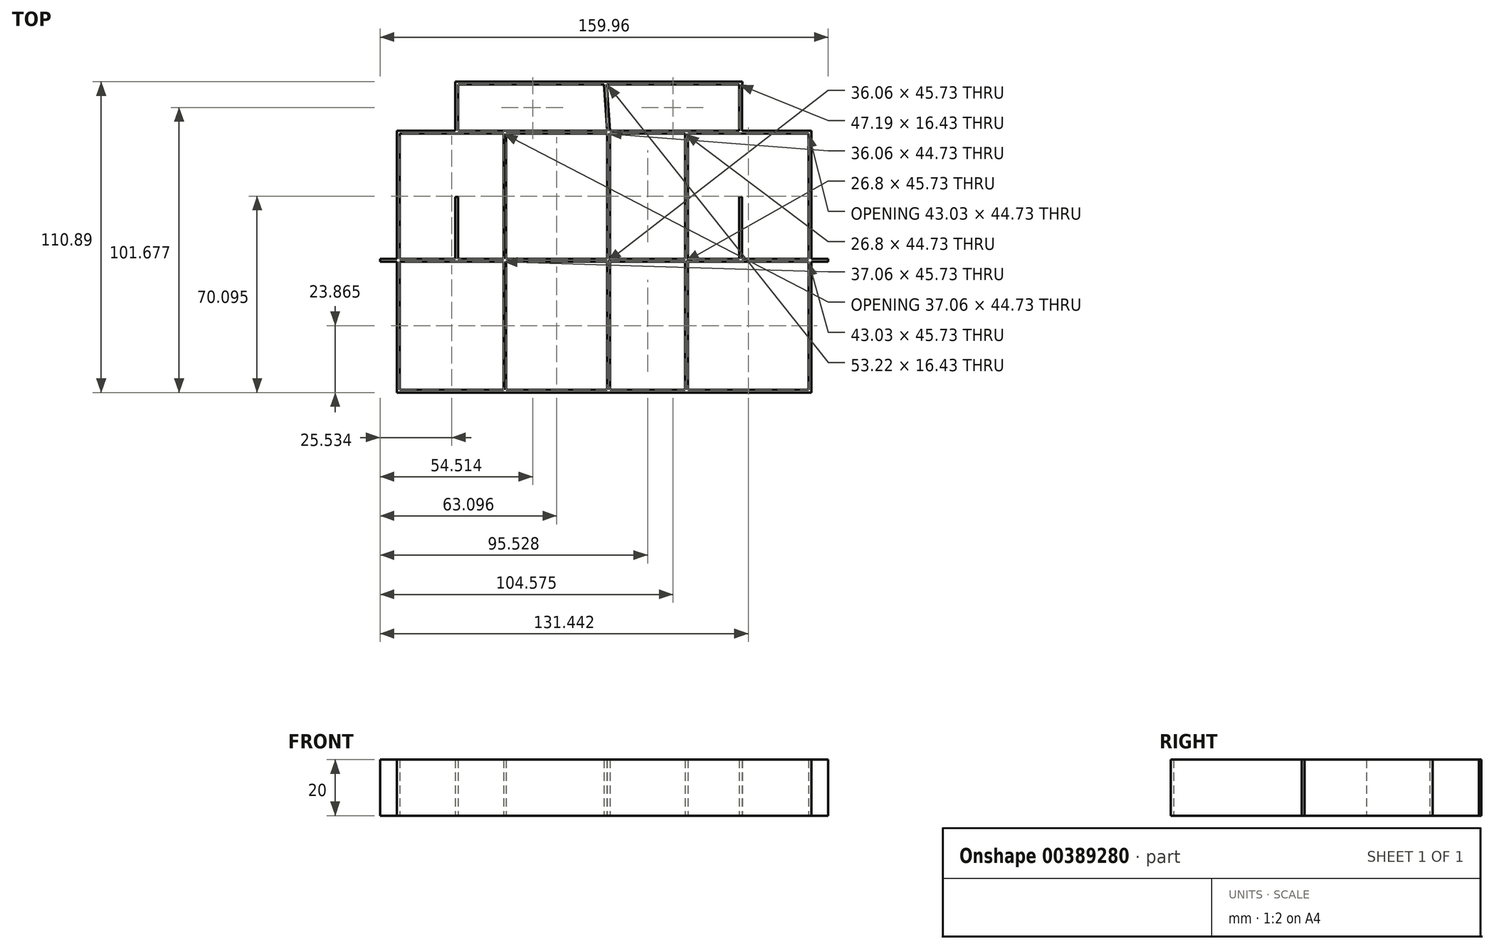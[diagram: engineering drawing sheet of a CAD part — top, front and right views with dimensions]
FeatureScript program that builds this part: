
annotation { "Feature Type Name" : "Feature", "Feature Type Description" : "" }
export const myFeature = defineFeature(function(context is Context, id is Id, definition is map)
    precondition{}
    {
        {
            var Q0;
            Q0=qCreatedBy(makeId("Top.planeOp"),FACE);
            var sketch = newSketch(context, id + "F0", { "sketchPlane" : qUnion([Q0])});
            skCircle(sketch, "E0", {"center": v(0, 0) * mm, "radius": 87.5 * mm});
            skLineSegment(sketch, "E1.bottom", {"start": v(-73.98, 46.73) * mm, "end": v(-53.08, 46.73) * mm});
            skLineSegment(sketch, "E1.top", {"start": v(-73.98, -46.73) * mm, "end": v(73.98, -46.73) * mm});
            skLineSegment(sketch, "E1.left", {"start": v(-73.98, 46.73) * mm, "end": v(-73.98, 1) * mm});
            skLineSegment(sketch, "E1.right", {"start": v(73.98, 46.73) * mm, "end": v(73.98, 1) * mm});
            skLineSegment(sketch, "E2.0", {"start": v(-72.98, 45.73) * mm, "end": v(-35.92, 45.73) * mm});
            skLineSegment(sketch, "E2.1", {"start": v(-72.98, 45.73) * mm, "end": v(-72.98, 1) * mm});
            skLineSegment(sketch, "E2.2", {"start": v(-72.98, -45.73) * mm, "end": v(-35.92, -45.73) * mm});
            skLineSegment(sketch, "E2.3", {"start": v(72.98, 45.73) * mm, "end": v(72.98, 1) * mm});
            skLineSegment(sketch, "E3.bottom", {"start": v(-72.98, 0) * mm, "end": v(-35.92, 0) * mm});
            skLineSegment(sketch, "E3.top", {"start": v(-72.98, 1) * mm, "end": v(-53.08, 1) * mm});
            skLineSegment(sketch, "E4.trimOffspring", {"start": v(-72.98, 0) * mm, "end": v(-72.98, -45.73) * mm});
            skLineSegment(sketch, "E5.trimOffspring", {"start": v(72.98, 0) * mm, "end": v(72.98, -45.73) * mm});
            skLineSegment(sketch, "E6.left", {"start": v(-53.08, 46.73) * mm, "end": v(-53.08, 63.16) * mm});
            skLineSegment(sketch, "E6.right", {"start": v(-52.08, 46.73) * mm, "end": v(-52.08, 63.16) * mm});
            skLineSegment(sketch, "E7.bottom", {"start": v(0, 63.16) * mm, "end": v(1, 63.16) * mm});
            skLineSegment(sketch, "E7.left", {"start": v(0, 63.16) * mm, "end": v(1.15, 46.73) * mm});
            skLineSegment(sketch, "E7.right", {"start": v(1, 63.16) * mm, "end": v(2.15, 46.73) * mm});
            skLineSegment(sketch, "E8.bottom", {"start": v(48.2, 63.16) * mm, "end": v(49.2, 63.16) * mm});
            skLineSegment(sketch, "E8.left", {"start": v(48.2, 63.16) * mm, "end": v(48.2, 46.73) * mm});
            skLineSegment(sketch, "E8.right", {"start": v(49.2, 63.16) * mm, "end": v(49.2, 46.73) * mm});
            skLineSegment(sketch, "E9.trimOffspring", {"start": v(-52.08, 46.73) * mm, "end": v(1.15, 46.73) * mm});
            skLineSegment(sketch, "E10.trimOffspring", {"start": v(2.15, 46.73) * mm, "end": v(48.2, 46.73) * mm});
            skLineSegment(sketch, "E11.trimOffspring", {"start": v(49.2, 46.73) * mm, "end": v(73.98, 46.73) * mm});
            skLineSegment(sketch, "E12.bottom", {"start": v(-73.98, 0) * mm, "end": v(-79.98, 0) * mm});
            skLineSegment(sketch, "E12.top", {"start": v(-73.98, 1) * mm, "end": v(-79.98, 1) * mm});
            skLineSegment(sketch, "E12.right", {"start": v(-79.98, 0) * mm, "end": v(-79.98, 1) * mm});
            skPoint(sketch, "E13.firstSnap0", {"position": v(73.98, 0) * mm});
            skPoint(sketch, "E13.oppositeSnap0", {"position": v(-76.98, 1) * mm});
            skLineSegment(sketch, "E13.bottom", {"start": v(73.98, 0) * mm, "end": v(79.98, 0) * mm});
            skLineSegment(sketch, "E13.top", {"start": v(73.98, 1) * mm, "end": v(79.98, 1) * mm});
            skLineSegment(sketch, "E13.right", {"start": v(79.98, 0) * mm, "end": v(79.98, 1) * mm});
            skLineSegment(sketch, "E14.trimOffspring", {"start": v(73.98, 0) * mm, "end": v(73.98, -46.73) * mm});
            skLineSegment(sketch, "E15.trimOffspring", {"start": v(-73.98, 0) * mm, "end": v(-73.98, -46.73) * mm});
            skLineSegment(sketch, "E16.left", {"start": v(1.15, 46.73) * mm, "end": v(1.15, -45.73) * mm});
            skLineSegment(sketch, "E16.right", {"start": v(2.15, 46.73) * mm, "end": v(2.15, -45.73) * mm});
            skLineSegment(sketch, "E17.trimOffspring", {"start": v(2.15, 45.73) * mm, "end": v(72.98, 45.73) * mm});
            skLineSegment(sketch, "E18.trimOffspring", {"start": v(2.15, 1) * mm, "end": v(28.95, 1) * mm});
            skLineSegment(sketch, "E19.trimOffspring", {"start": v(2.15, 0) * mm, "end": v(28.95, 0) * mm});
            skLineSegment(sketch, "E20.trimOffspring", {"start": v(2.15, -45.73) * mm, "end": v(28.95, -45.73) * mm});
            skLineSegment(sketch, "E21.top", {"start": v(-53.08, 23.07) * mm, "end": v(-52.08, 23.07) * mm});
            skLineSegment(sketch, "E21.left", {"start": v(-53.08, 1) * mm, "end": v(-53.08, 23.07) * mm});
            skLineSegment(sketch, "E21.right", {"start": v(-52.08, 1) * mm, "end": v(-52.08, 23.07) * mm});
            skLineSegment(sketch, "E22.top", {"start": v(49.2, 23.07) * mm, "end": v(48.2, 23.07) * mm});
            skLineSegment(sketch, "E22.left", {"start": v(49.2, 1) * mm, "end": v(49.2, 23.07) * mm});
            skLineSegment(sketch, "E22.right", {"start": v(48.2, 1) * mm, "end": v(48.2, 23.07) * mm});
            skLineSegment(sketch, "E23.trimOffspring", {"start": v(-52.08, 1) * mm, "end": v(-35.92, 1) * mm});
            skLineSegment(sketch, "E24.trimOffspring", {"start": v(49.2, 1) * mm, "end": v(72.98, 1) * mm});
            skLineSegment(sketch, "E25.bottom", {"start": v(-52.08, 63.16) * mm, "end": v(49.41, 63.16) * mm});
            skLineSegment(sketch, "E25.top", {"start": v(-53.08, 64.16) * mm, "end": v(49.41, 64.16) * mm});
            skLineSegment(sketch, "E25.left", {"start": v(-53.08, 63.16) * mm, "end": v(-53.08, 64.16) * mm});
            skLineSegment(sketch, "E25.right", {"start": v(49.41, 63.16) * mm, "end": v(49.41, 64.16) * mm});
            skLineSegment(sketch, "E26.left", {"start": v(-35.92, 45.73) * mm, "end": v(-35.92, -45.73) * mm});
            skLineSegment(sketch, "E26.right", {"start": v(-34.92, 45.73) * mm, "end": v(-34.92, -45.73) * mm});
            skLineSegment(sketch, "E27.bottom", {"start": v(28.95, 45.73) * mm, "end": v(29.95, 45.73) * mm});
            skLineSegment(sketch, "E27.left", {"start": v(28.95, 45.73) * mm, "end": v(28.95, 1) * mm});
            skLineSegment(sketch, "E27.right", {"start": v(29.95, 45.73) * mm, "end": v(29.95, 1) * mm});
            skLineSegment(sketch, "E28.trimOffspring", {"start": v(-34.92, 45.73) * mm, "end": v(1.15, 45.73) * mm});
            skLineSegment(sketch, "E29.trimOffspring", {"start": v(-34.92, 1) * mm, "end": v(1.15, 1) * mm});
            skLineSegment(sketch, "E30.trimOffspring", {"start": v(-34.92, 0) * mm, "end": v(0, 0) * mm});
            skLineSegment(sketch, "E31.trimOffspring", {"start": v(-34.92, -45.73) * mm, "end": v(1.15, -45.73) * mm});
            skLineSegment(sketch, "E32.trimOffspring", {"start": v(29.95, -45.73) * mm, "end": v(72.98, -45.73) * mm});
            skLineSegment(sketch, "E33.trimOffspring", {"start": v(29.95, 1) * mm, "end": v(48.2, 1) * mm});
            skLineSegment(sketch, "E34.trimOffspring", {"start": v(28.95, 0) * mm, "end": v(28.95, -45.73) * mm});
            skLineSegment(sketch, "E35.trimOffspring", {"start": v(29.95, 0) * mm, "end": v(72.98, 0) * mm});
            skLineSegment(sketch, "E36.trimOffspring", {"start": v(29.95, 0) * mm, "end": v(29.95, -45.73) * mm});
            skLineSegment(sketch, "E37", {"start": v(0, 0) * mm, "end": v(1.15, 0) * mm});
            skPoint(sketch, "E37.endSnap0", {"position": v(1.15, 0.5) * mm});
            skSolve(sketch);
        }
        {
            var Q0;
            {var subQ0=sQuery(id+"F0.wireOp",EDGE,"E1.bottom");var subQ1=sQuery(id+"F0.wireOp",EDGE,"E0");var subQ2=makeQuery(id+"F0.imprint","INTERSECT",VERTEX,{"derivedFrom":[subQ1,subQ0]});Q0=makeQuery(id+"F0.imprint","IMPRINT",FACE,{"disambiguationData":[TD([[makeQuery(id+"F0.imprint","IMPRINT",EDGE,{"disambiguationData":[TD([[subQ2,1.0]])],"derivedFrom":subQ1}),-1.0]])]});}
            var Q1;
            {var subQ1=sQuery(id+"F0.wireOp",EDGE,"E1.top");Q1=makeQuery(id+"F0.imprint","IMPRINT",FACE,{"disambiguationData":[TD([[makeQuery(id+"F0.imprint","IMPRINT",EDGE,{"derivedFrom":subQ1}),1.0]])]});}
            var Q2;
            {var subQ1=sQuery(id+"F0.wireOp",EDGE,"E29.trimOffspring");Q2=makeQuery(id+"F0.imprint","IMPRINT",FACE,{"disambiguationData":[TD([[makeQuery(id+"F0.imprint","IMPRINT",EDGE,{"derivedFrom":subQ1}),-1.0]])]});}
            extrude(context, id + "F1", {"entities" : qUnion([Q0, Q1, Q2]), "depth" : 20 * mm, "offsetDistance" : 25 * mm});
        }
    });
